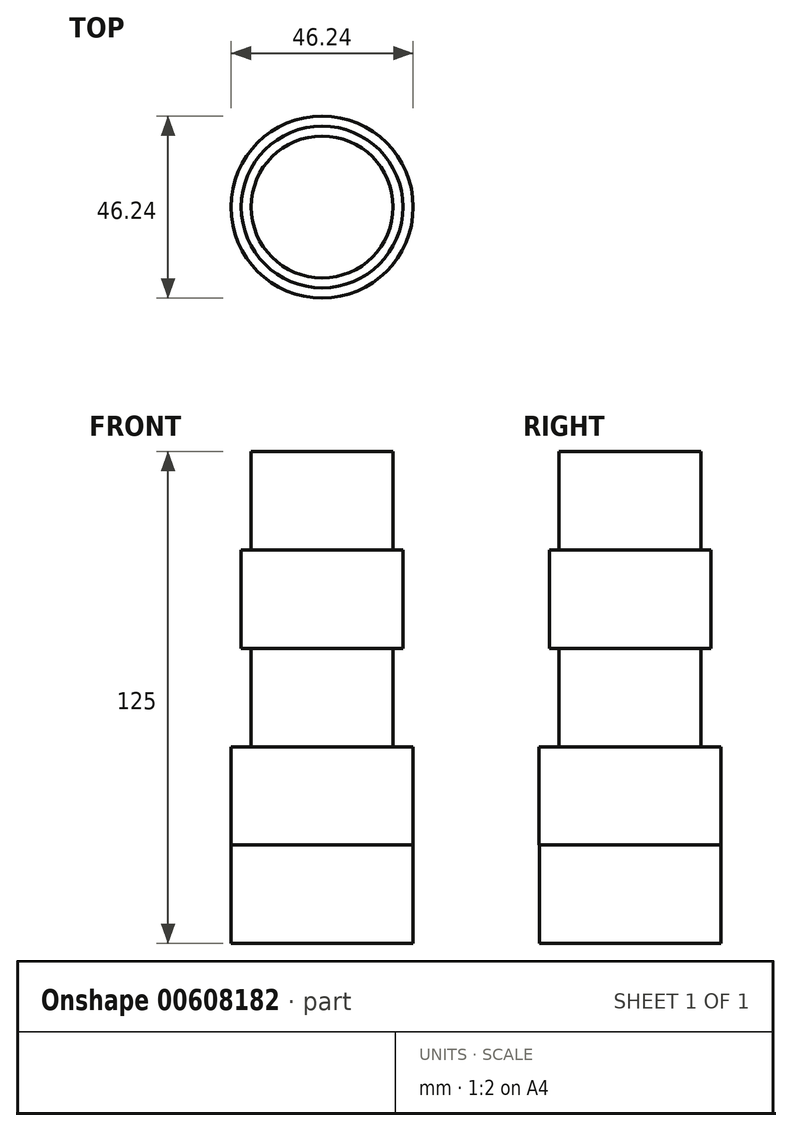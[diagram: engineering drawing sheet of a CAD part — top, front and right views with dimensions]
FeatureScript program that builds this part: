
annotation { "Feature Type Name" : "Feature", "Feature Type Description" : "" }
export const myFeature = defineFeature(function(context is Context, id is Id, definition is map)
    precondition{}
    {
        {
            var Q0;
            Q0=qCreatedBy(makeId("Top.planeOp"),FACE);
            var sketch = newSketch(context, id + "F0", { "sketchPlane" : qUnion([Q0])});
            skCircle(sketch, "E0", {"center": v(0, 0) * mm, "radius": 23.08 * mm});
            skSolve(sketch);
        }
        {
            var Q0;
            Q0 = qSketchRegion(id + "F0", true);
            extrude(context, id + "F1", {"entities" : qUnion([Q0]), "depth" : 25 * mm, "offsetDistance" : 25 * mm});
        }
        {
            var Q0;
            Q0=makeQuery(id+"F1.opExtrude","CAP_FACE",FACE,{"disambiguationData":[OSD([sQuery(id+"F0.wireOp",EDGE,"E0")])],"isStart":false});
            var sketch = newSketch(context, id + "F2", { "sketchPlane" : qUnion([Q0])});
            skCircle(sketch, "E1", {"center": v(0, 0) * mm, "radius": 23.11 * mm});
            skSolve(sketch);
        }
        {
            var Q0;
            Q0 = qSketchRegion(id + "F2", true);
            extrude(context, id + "F3", {"entities" : qUnion([Q0]), "operationType" : NewBodyOperationType.ADD, "depth" : 25 * mm, "offsetDistance" : 25 * mm});
        }
        {
            var Q0;
            Q0=makeQuery(id+"F3.opExtrude","CAP_FACE",FACE,{"disambiguationData":[OSD([sQuery(id+"F2.wireOp",EDGE,"E1")])],"isStart":false});
            var sketch = newSketch(context, id + "F4", { "sketchPlane" : qUnion([Q0])});
            skCircle(sketch, "E2", {"center": v(0, 0) * mm, "radius": 18.03 * mm});
            skSolve(sketch);
        }
        {
            var Q0;
            Q0 = qSketchRegion(id + "F4", true);
            extrude(context, id + "F5", {"entities" : qUnion([Q0]), "operationType" : NewBodyOperationType.ADD, "depth" : 25 * mm, "offsetDistance" : 25 * mm});
        }
        {
            var Q0;
            Q0=makeQuery(id+"F5.opExtrude","CAP_FACE",FACE,{"disambiguationData":[OSD([sQuery(id+"F4.wireOp",EDGE,"E2")])],"isStart":false});
            var sketch = newSketch(context, id + "F6", { "sketchPlane" : qUnion([Q0])});
            skCircle(sketch, "E3", {"center": v(0, 0) * mm, "radius": 20.54 * mm});
            skSolve(sketch);
        }
        {
            var Q0;
            Q0 = qSketchRegion(id + "F6", true);
            extrude(context, id + "F7", {"entities" : qUnion([Q0]), "operationType" : NewBodyOperationType.ADD, "depth" : 25 * mm, "offsetDistance" : 25 * mm});
        }
        {
            var Q0;
            Q0=makeQuery(id+"F7.opExtrude","CAP_FACE",FACE,{"disambiguationData":[OSD([sQuery(id+"F6.wireOp",EDGE,"E3")])],"isStart":false});
            var sketch = newSketch(context, id + "F8", { "sketchPlane" : qUnion([Q0])});
            skCircle(sketch, "E4", {"center": v(0, 0) * mm, "radius": 18.03 * mm});
            skSolve(sketch);
        }
        {
            var Q0;
            Q0 = qSketchRegion(id + "F8", true);
            extrude(context, id + "F9", {"entities" : qUnion([Q0]), "operationType" : NewBodyOperationType.ADD, "depth" : 25 * mm, "offsetDistance" : 25 * mm});
        }
    });
